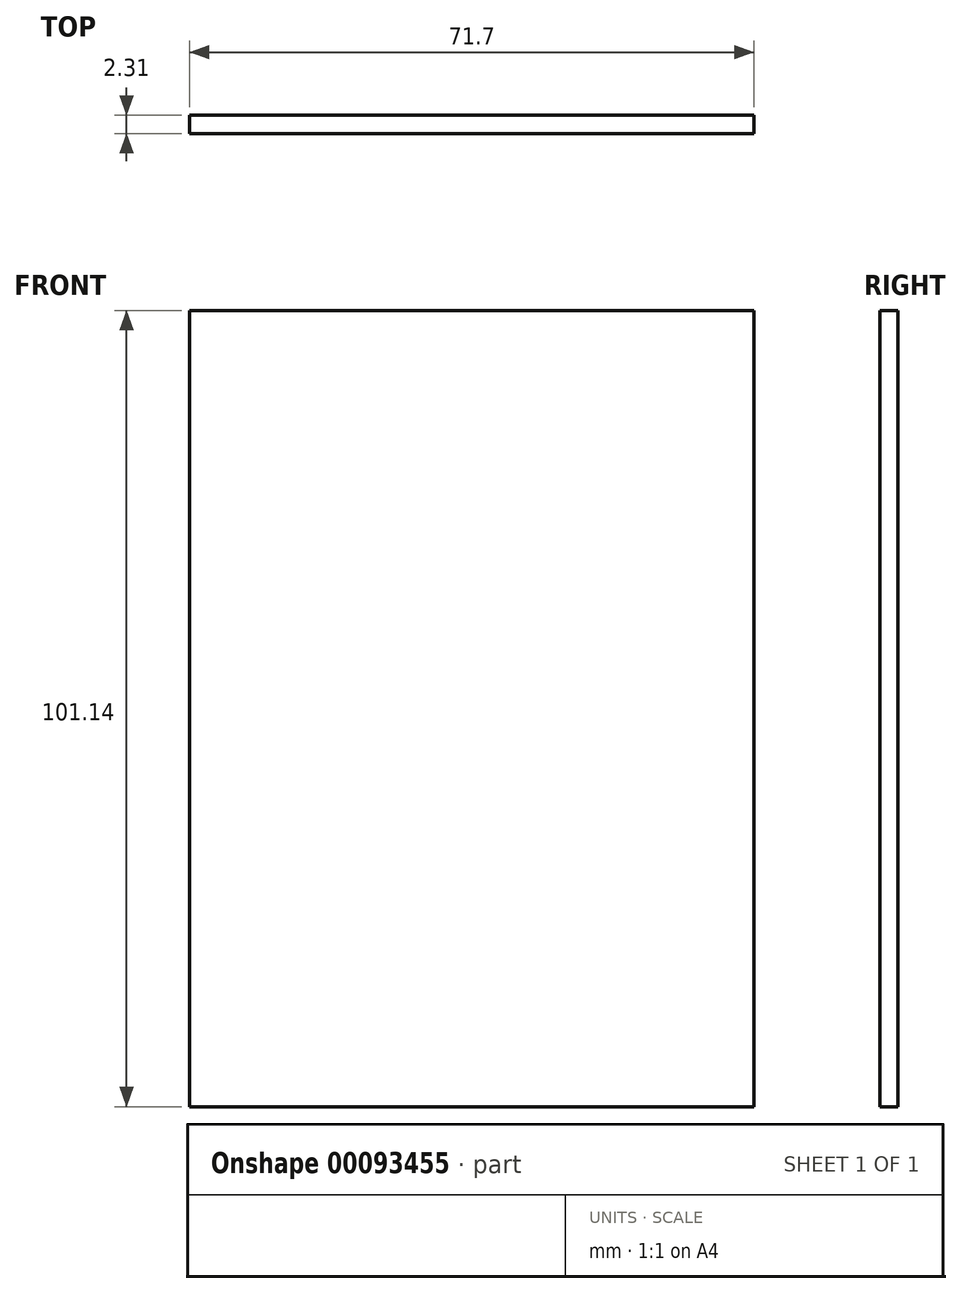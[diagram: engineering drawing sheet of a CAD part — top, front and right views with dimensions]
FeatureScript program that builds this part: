
annotation { "Feature Type Name" : "Feature", "Feature Type Description" : "" }
export const myFeature = defineFeature(function(context is Context, id is Id, definition is map)
    precondition{}
    {
        {
            var Q0;
            Q0=qCreatedBy(makeId("Front.planeOp"),FACE);
            var sketch = newSketch(context, id + "F0", { "sketchPlane" : qUnion([Q0])});
            skLineSegment(sketch, "E0.bottom", {"start": v(-35.68, 65.8) * mm, "end": v(36.02, 65.8) * mm});
            skLineSegment(sketch, "E0.top", {"start": v(-35.68, -35.33) * mm, "end": v(36.02, -35.33) * mm});
            skLineSegment(sketch, "E0.left", {"start": v(-35.68, 65.8) * mm, "end": v(-35.68, -35.33) * mm});
            skLineSegment(sketch, "E0.right", {"start": v(36.02, 65.8) * mm, "end": v(36.02, -35.33) * mm});
            skSolve(sketch);
        }
        {
            var Q0;
            Q0=makeQuery(id+"F0.imprint","IMPRINT",FACE,{"disambiguationData":[TD([[makeQuery(id+"F0.imprint","IMPRINT",EDGE,{"derivedFrom":sQuery(id+"F0.wireOp",EDGE,"E0.bottom")}),-1.0]])]});
            extrude(context, id + "F1", {"entities" : qUnion([Q0]), "oppositeDirection" : true, "depth" : 2.3 * mm});
        }
    });
